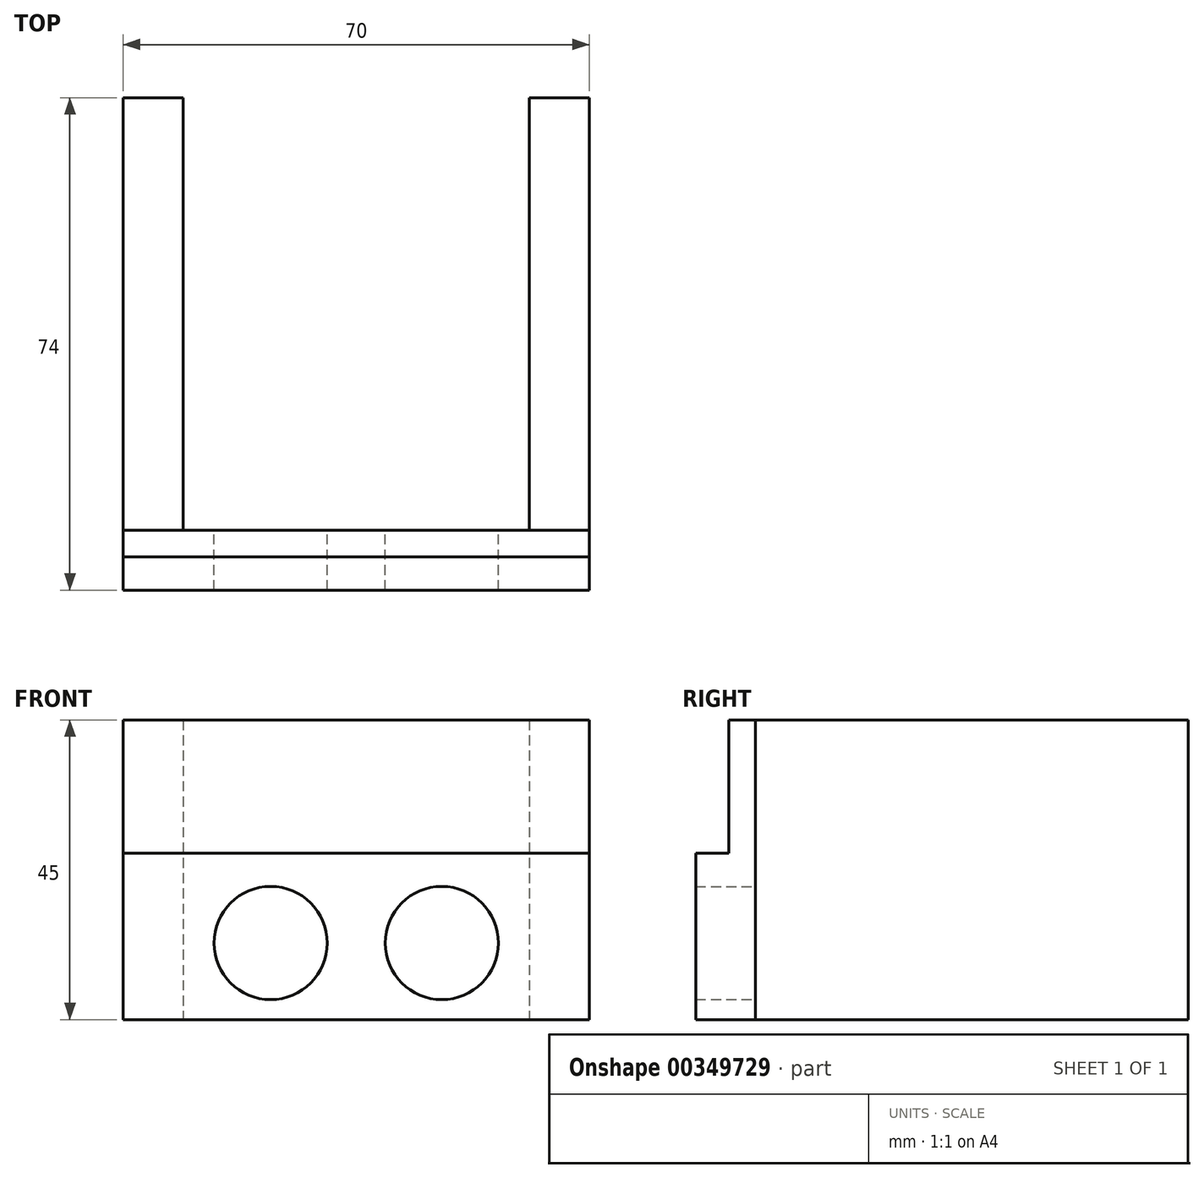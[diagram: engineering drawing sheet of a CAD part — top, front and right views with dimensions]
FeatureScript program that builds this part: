
annotation { "Feature Type Name" : "Feature", "Feature Type Description" : "" }
export const myFeature = defineFeature(function(context is Context, id is Id, definition is map)
    precondition{}
    {
        {
            var Q0;
            Q0=qCreatedBy(makeId("Front.planeOp"),FACE);
            var sketch = newSketch(context, id + "F0", { "sketchPlane" : qUnion([Q0])});
            skLineSegment(sketch, "E0.bottom", {"start": v(-35, 33.5) * mm, "end": v(35, 33.5) * mm});
            skLineSegment(sketch, "E0.top", {"start": v(-35, -11.5) * mm, "end": v(35, -11.5) * mm});
            skLineSegment(sketch, "E0.left", {"start": v(-35, 33.5) * mm, "end": v(-35, -11.5) * mm});
            skLineSegment(sketch, "E0.right", {"start": v(35, 33.5) * mm, "end": v(35, -11.5) * mm});
            skCircle(sketch, "E1", {"center": v(-12.85, 0) * mm, "radius": 8.5 * mm});
            skCircle(sketch, "E2.MirrorC", {"center": v(12.85, 0) * mm, "radius": 8.5 * mm});
            skSolve(sketch);
        }
        {
            var Q0;
            Q0=makeQuery(id+"F0.imprint","IMPRINT",FACE,{"disambiguationData":[TD([[makeQuery(id+"F0.imprint","IMPRINT",EDGE,{"derivedFrom":sQuery(id+"F0.wireOp",EDGE,"E0.bottom")}),-1.0]])]});
            extrude(context, id + "F1", {"entities" : qUnion([Q0]), "depth" : 9 * mm});
        }
        {
            var Q0;
            Q0=makeQuery(id+"F1.opExtrude","CAP_FACE",FACE,{"disambiguationData":[OSD([sQuery(id+"F0.wireOp",EDGE,"E0.bottom"),sQuery(id+"F0.wireOp",EDGE,"E0.top"),sQuery(id+"F0.wireOp",EDGE,"E0.left"),sQuery(id+"F0.wireOp",EDGE,"E0.right"),sQuery(id+"F0.wireOp",EDGE,"E1"),sQuery(id+"F0.wireOp",EDGE,"E2.MirrorC")])],"isStart":false});
            var sketch = newSketch(context, id + "F2", { "sketchPlane" : qUnion([Q0])});
            skLineSegment(sketch, "E3.bottom", {"start": v(-35, 33.5) * mm, "end": v(35, 33.5) * mm});
            skLineSegment(sketch, "E3.top", {"start": v(-35, 13.5) * mm, "end": v(35, 13.5) * mm});
            skLineSegment(sketch, "E3.left", {"start": v(-35, 33.5) * mm, "end": v(-35, 13.5) * mm});
            skLineSegment(sketch, "E3.right", {"start": v(35, 33.5) * mm, "end": v(35, 13.5) * mm});
            skSolve(sketch);
        }
        {
            var Q0;
            Q0 = qSketchRegion(id + "F2", true);
            extrude(context, id + "F3", {"entities" : qUnion([Q0]), "operationType" : NewBodyOperationType.REMOVE, "oppositeDirection" : true, "depth" : 5 * mm});
        }
        {
            var Q0;
            Q0=makeQuery(id+"F1.opExtrude","SWEPT_FACE",FACE,{"disambiguationData":[OSD([sQuery(id+"F0.wireOp",EDGE,"E0.right")])]});
            var sketch = newSketch(context, id + "F4", { "sketchPlane" : qUnion([Q0])});
            skLineSegment(sketch, "E4.bottom", {"start": v(0, 33.5) * mm, "end": v(65, 33.5) * mm});
            skLineSegment(sketch, "E4.top", {"start": v(0, -11.5) * mm, "end": v(65, -11.5) * mm});
            skLineSegment(sketch, "E4.left", {"start": v(0, 33.5) * mm, "end": v(0, -11.5) * mm});
            skLineSegment(sketch, "E4.right", {"start": v(65, 33.5) * mm, "end": v(65, -11.5) * mm});
            skSolve(sketch);
        }
        {
            var Q0;
            Q0=makeQuery(id+"F4.imprint","IMPRINT",FACE,{"disambiguationData":[TD([[makeQuery(id+"F4.imprint","IMPRINT",EDGE,{"derivedFrom":sQuery(id+"F4.wireOp",EDGE,"E4.bottom")}),-1.0]])]});
            extrude(context, id + "F5", {"entities" : qUnion([Q0]), "oppositeDirection" : true, "depth" : 9 * mm});
        }
        {
            var Q0;
            Q0=makeQuery(id+"F5.opExtrude","SWEPT_BODY",BODY,{"disambiguationData":[OSD([sQuery(id+"F4.wireOp",EDGE,"E4.bottom"),sQuery(id+"F4.wireOp",EDGE,"E4.top"),sQuery(id+"F4.wireOp",EDGE,"E4.left"),sQuery(id+"F4.wireOp",EDGE,"E4.right")])]});
            var Q1;
            Q1=qCreatedBy(makeId("Right.planeOp"),FACE);
            mirror(context, id + "F6", {"entities" : qUnion([Q0]), "mirrorPlane" : qUnion([Q1])});
        }
    });
